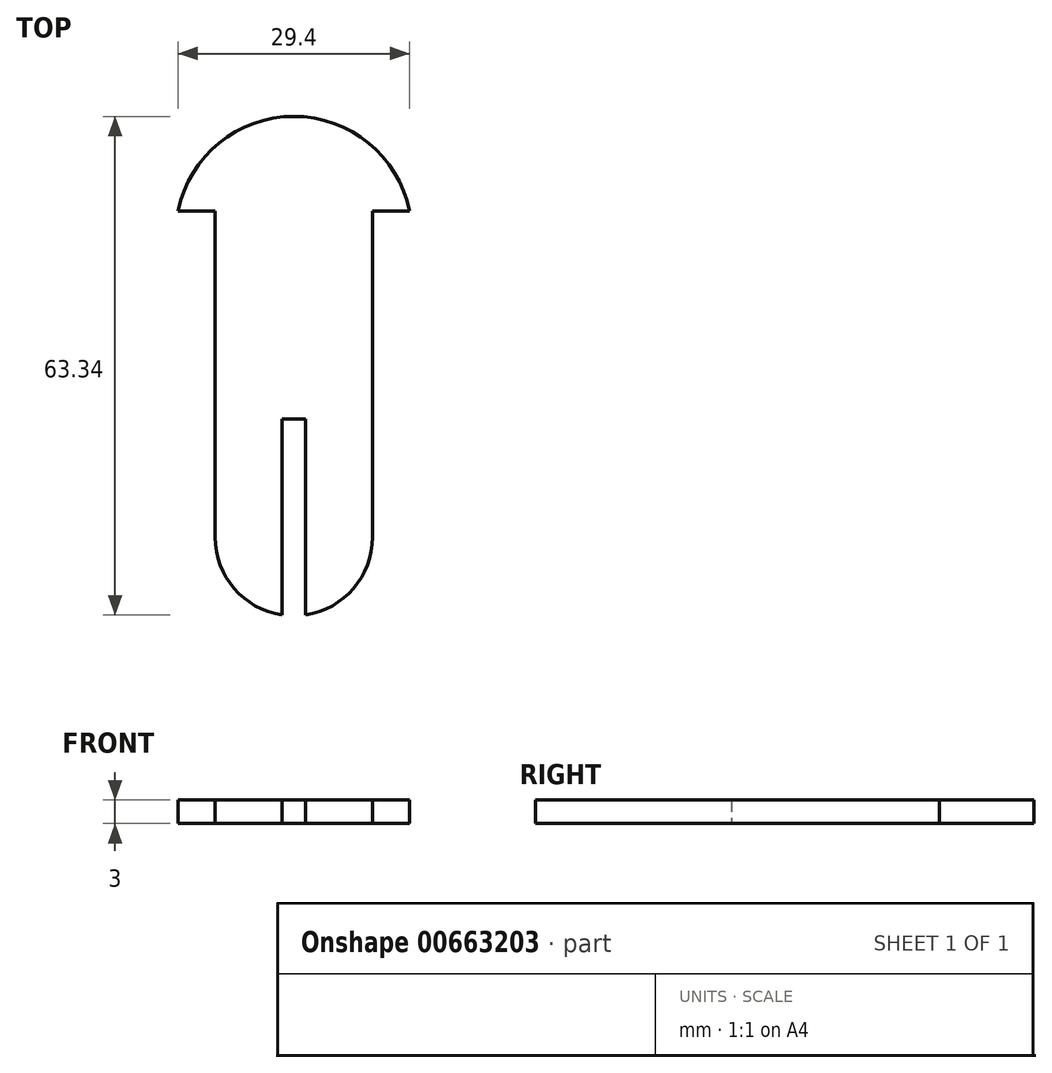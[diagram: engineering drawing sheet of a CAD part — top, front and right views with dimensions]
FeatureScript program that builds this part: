
annotation { "Feature Type Name" : "Feature", "Feature Type Description" : "" }
export const myFeature = defineFeature(function(context is Context, id is Id, definition is map)
    precondition{}
    {
        {
            var Q0;
            Q0=qCreatedBy(makeId("Top.planeOp"),FACE);
            var sketch = newSketch(context, id + "F0", { "sketchPlane" : qUnion([Q0])});
            skLineSegment(sketch, "E0.bottom", {"start": v(-10, 20.73) * mm, "end": v(10, 20.73) * mm});
            skLineSegment(sketch, "E0.top", {"start": v(-10, -20.73) * mm, "end": v(10, -20.73) * mm});
            skLineSegment(sketch, "E0.left", {"start": v(-10, 20.73) * mm, "end": v(-10, -20.73) * mm});
            skLineSegment(sketch, "E0.right", {"start": v(10, 20.73) * mm, "end": v(10, -20.73) * mm});
            skPoint(sketch, "E0.middle", {"position": v(0, 0) * mm});
            skArc(sketch, "E1", {"start": v(-14.7, 20.72) * mm, "mid": v(0, 32.72) * mm, "end": v(14.7, 20.72) * mm});
            skLineSegment(sketch, "E2", {"start": v(10, 20.73) * mm, "end": v(14.7, 20.73) * mm});
            skLineSegment(sketch, "E3", {"start": v(-10, 20.73) * mm, "end": v(-14.7, 20.72) * mm});
            skArc(sketch, "E4", {"start": v(-10, -20.73) * mm, "mid": v(0, -30.73) * mm, "end": v(10, -20.73) * mm});
            skLineSegment(sketch, "E5.bottom", {"start": v(-1.5, -5.72) * mm, "end": v(1.5, -5.72) * mm});
            skLineSegment(sketch, "E5.top", {"start": v(-1.5, -35.72) * mm, "end": v(1.5, -35.72) * mm});
            skLineSegment(sketch, "E5.left", {"start": v(-1.5, -5.73) * mm, "end": v(-1.5, -35.73) * mm});
            skLineSegment(sketch, "E5.right", {"start": v(1.5, -5.73) * mm, "end": v(1.5, -35.73) * mm});
            skSolve(sketch);
        }
        {
            var Q0;
            Q0=makeQuery(id+"F0.imprint","IMPRINT",FACE,{"disambiguationData":[TD([[makeQuery(id+"F0.imprint","IMPRINT",EDGE,{"derivedFrom":sQuery(id+"F0.wireOp",EDGE,"E0.bottom")}),-1.0]])]});
            var Q1;
            Q1=makeQuery(id+"F0.imprint","IMPRINT",FACE,{"disambiguationData":[TD([[makeQuery(id+"F0.imprint","IMPRINT",EDGE,{"derivedFrom":sQuery(id+"F0.wireOp",EDGE,"E0.bottom")}),1.0]])]});
            var Q2;
            {var subQ0=sQuery(id+"F0.wireOp",EDGE,"E4");var subQ3=sQuery(id+"F0.wireOp",EDGE,"E5.left");var subQ5=makeQuery(id+"F0.imprint","INTERSECT",VERTEX,{"derivedFrom":[subQ0,subQ3]});Q2=makeQuery(id+"F0.imprint","IMPRINT",FACE,{"disambiguationData":[TD([[makeQuery(id+"F0.imprint","IMPRINT",EDGE,{"disambiguationData":[TD([[subQ5,1.0]])],"derivedFrom":subQ3}),-1.0]])]});}
            var Q3;
            {var subQ0=sQuery(id+"F0.wireOp",EDGE,"E4");var subQ3=sQuery(id+"F0.wireOp",EDGE,"E5.right");var subQ5=makeQuery(id+"F0.imprint","INTERSECT",VERTEX,{"derivedFrom":[subQ0,subQ3]});Q3=makeQuery(id+"F0.imprint","IMPRINT",FACE,{"disambiguationData":[TD([[makeQuery(id+"F0.imprint","IMPRINT",EDGE,{"disambiguationData":[TD([[subQ5,1.0]])],"derivedFrom":subQ3}),1.0]])]});}
            extrude(context, id + "F1", {"entities" : qUnion([Q0, Q1, Q2, Q3]), "depth" : 3 * mm, "offsetDistance" : 25 * mm});
        }
    });
